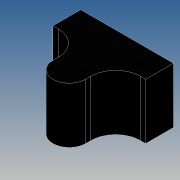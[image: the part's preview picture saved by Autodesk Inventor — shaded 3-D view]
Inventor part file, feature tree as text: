
AUTODESK INVENTOR PART (.ipt)
format: ipt  version: 2016 (Build 200138000, 138)  size: 147,456 bytes
history: native  units: mm
features: sketch x3, extrude x2, shell x1
ambient origin geometry x8: Origin, YZ Plane, XZ Plane, XY Plane, X Axis, Y Axis, Z Axis, Center Point
bodies: Solid1 (feature_tree)
feature tree (6):
  extrude  "Extrusion1"  Depth=4.5mm
  shell  "Shell1"  Thickness=15.0mm
  extrude  "Extrusion2"  Depth=4.0mm
  sketch  "Sketch2"  dims[d3=12.0mm d4=4.0mm]
  sketch  "Sketch1"  dims[d0=2.65mm d1=4.5mm d2=15.0mm]
  sketch  "Sketch3"  dims[d5=9.0mm d6=0.0mm d7=1.0mm d8=1.2mm d9=7.0mm d10=4.8mm d11=0.8mm d12=9.0mm d13=0.0mm]
